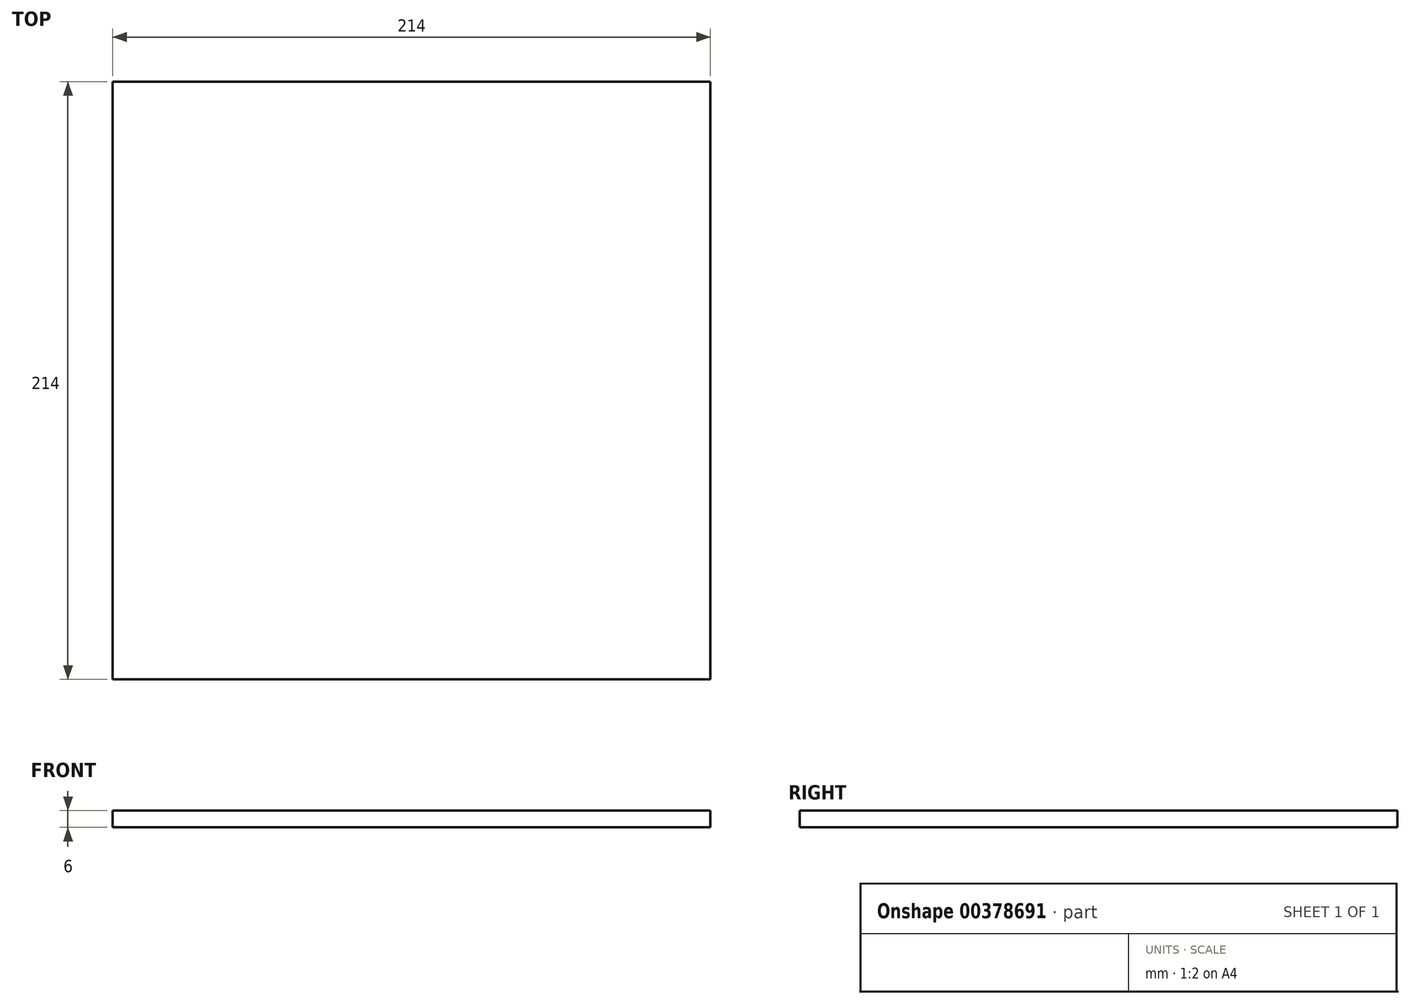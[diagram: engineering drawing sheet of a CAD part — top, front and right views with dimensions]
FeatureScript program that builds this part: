
annotation { "Feature Type Name" : "Feature", "Feature Type Description" : "" }
export const myFeature = defineFeature(function(context is Context, id is Id, definition is map)
    precondition{}
    {
        {
            var Q0;
            Q0=qCreatedBy(makeId("Top.planeOp"),FACE);
            var sketch = newSketch(context, id + "F0", { "sketchPlane" : qUnion([Q0])});
            skLineSegment(sketch, "E0.bottom", {"start": v(0, 0) * mm, "end": v(214, 0) * mm});
            skLineSegment(sketch, "E0.top", {"start": v(0, 214) * mm, "end": v(214, 214) * mm});
            skLineSegment(sketch, "E0.left", {"start": v(0, 0) * mm, "end": v(0, 214) * mm});
            skLineSegment(sketch, "E0.right", {"start": v(214, 0) * mm, "end": v(214, 214) * mm});
            skSolve(sketch);
        }
        {
            var Q0;
            Q0=qSketchRegion(id+"F0",true);
            extrude(context, id + "F1", {"entities" : qUnion([Q0]), "depth" : 6 * mm});
        }
    });
